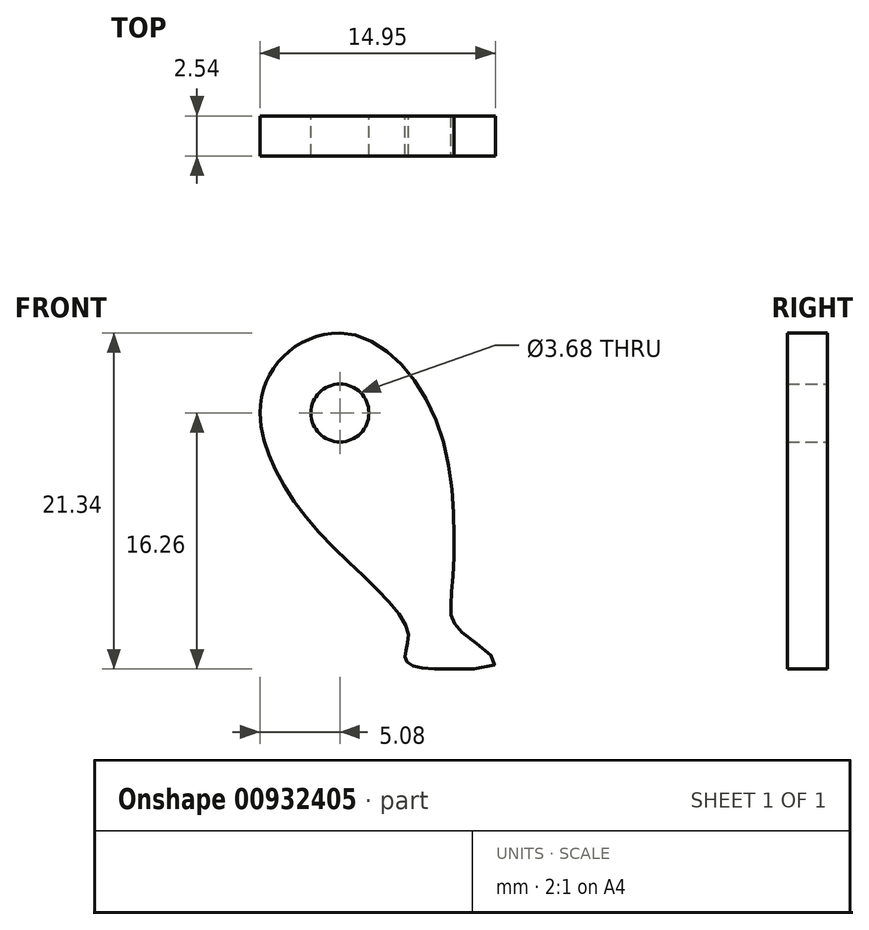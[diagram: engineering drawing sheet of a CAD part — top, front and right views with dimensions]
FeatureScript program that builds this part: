
annotation { "Feature Type Name" : "Feature", "Feature Type Description" : "" }
export const myFeature = defineFeature(function(context is Context, id is Id, definition is map)
    precondition{}
    {
        {
            var Q0;
            Q0=qCreatedBy(makeId("Front.planeOp"),FACE);
            var sketch = newSketch(context, id + "F0", { "sketchPlane" : qUnion([Q0])});
            skCircle(sketch, "E0", {"center": v(0, 0) * mm, "radius": 1.84 * mm});
            skLineSegment(sketch, "E1", {"start": v(6, -16.26) * mm, "end": v(8.5, -16.26) * mm});
            skArc(sketch, "E2", {"start": v(-5.08, 0) * mm, "mid": v(-3.6, 3.6) * mm, "end": v(0, 5.08) * mm});
            skFitSpline(sketch, "E3", {"points": [v(0, 5.08) * mm, v(6.19, -0.67) * mm, v(7.07, -11.71) * mm, v(8.16, -14.27) * mm, v(8.5, -16.26) * mm], "startDerivative": vector(22.9, 0) * mm, "endDerivative": vector(-53.6, 0) * mm});
            skFitSpline(sketch, "E4", {"points": [v(-5.08, 0) * mm, v(-1.65, -7.21) * mm, v(4.32, -13.9) * mm, v(4.13, -15.55) * mm, v(6, -16.26) * mm], "startDerivative": vector(0, -18.73) * mm, "endDerivative": vector(20.02, 0) * mm});
            skSolve(sketch);
        }
        {
            var Q0;
            Q0=makeQuery(id+"F0.imprint","IMPRINT",FACE,{"disambiguationData":[TD([[makeQuery(id+"F0.imprint","IMPRINT",EDGE,{"derivedFrom":sQuery(id+"F0.wireOp",EDGE,"E0")}),-1.0]])]});
            extrude(context, id + "F1", {"entities" : qUnion([Q0]), "depth" : 2.54 * mm, "offsetDistance" : 25 * mm});
        }
    });
